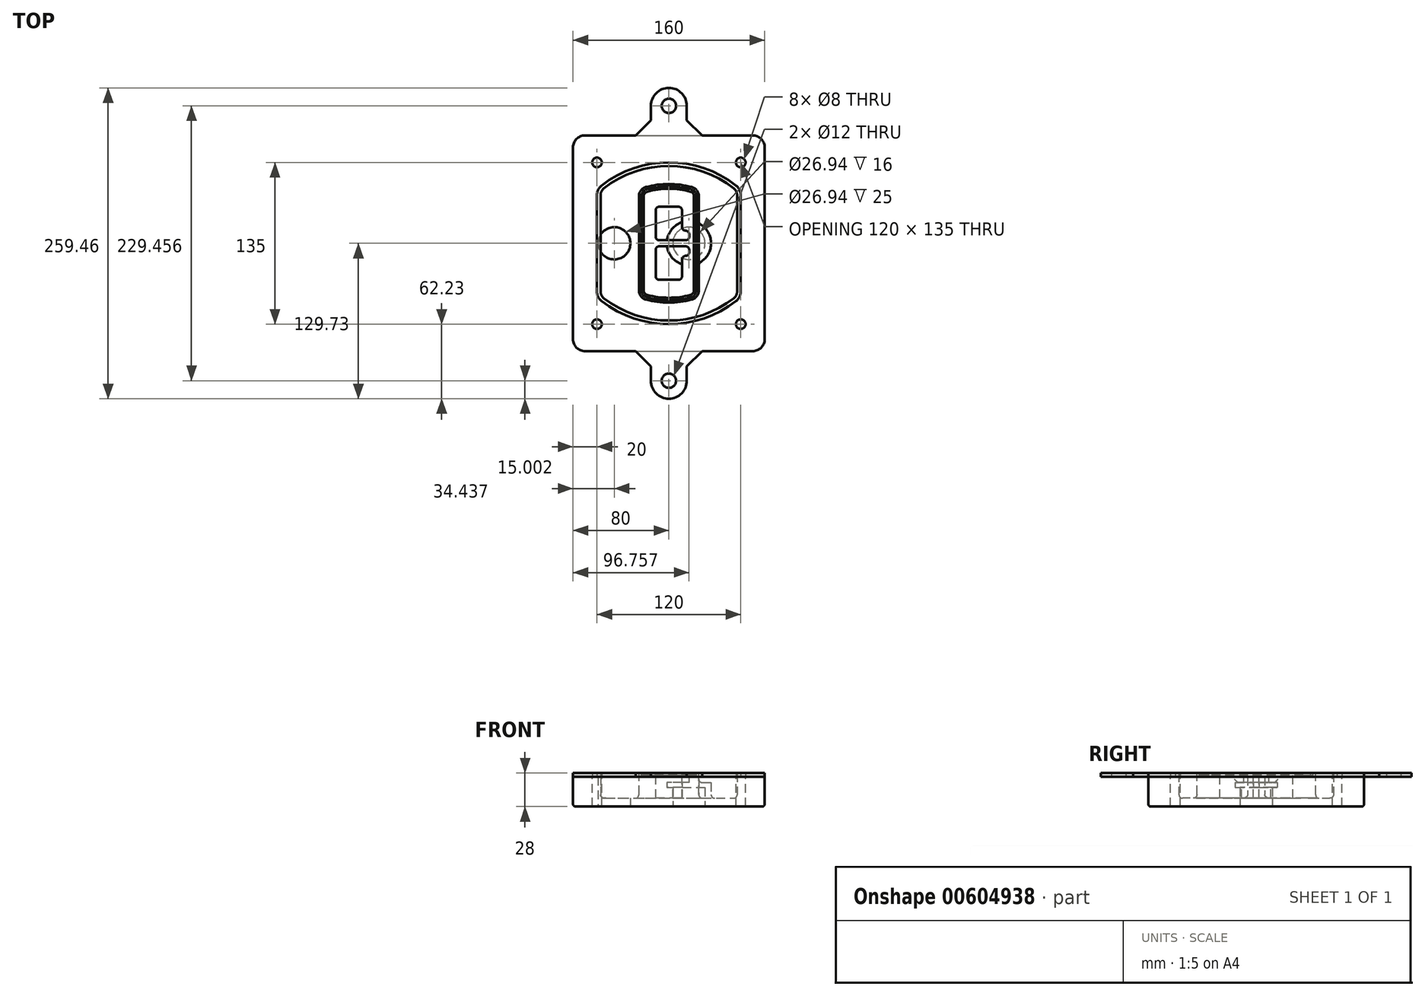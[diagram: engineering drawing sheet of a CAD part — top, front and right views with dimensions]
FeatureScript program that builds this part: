
annotation { "Feature Type Name" : "Feature", "Feature Type Description" : "" }
export const myFeature = defineFeature(function(context is Context, id is Id, definition is map)
    precondition{}
    {
        {
            var Q0;
            Q0=qCreatedBy(makeId("Top.planeOp"),FACE);
            var sketch = newSketch(context, id + "F0", { "sketchPlane" : qUnion([Q0])});
            skPoint(sketch, "E0.rect.middle", {"position": v(0, 0) * mm});
            skLineSegment(sketch, "E1.bottom", {"start": v(-70, -90) * mm, "end": v(70, -90) * mm});
            skLineSegment(sketch, "E1.top", {"start": v(-70, 90) * mm, "end": v(70, 90) * mm});
            skLineSegment(sketch, "E1.left", {"start": v(-80, -80) * mm, "end": v(-80, 80) * mm});
            skLineSegment(sketch, "E1.right", {"start": v(80, -80) * mm, "end": v(80, 80) * mm});
            skLineSegment(sketch, "E2", {"start": v(-80, 90) * mm, "end": v(80, -90) * mm, "construction": true});
            skLineSegment(sketch, "E3", {"start": v(80, 90) * mm, "end": v(-80, -90) * mm, "construction": true});
            skCircle(sketch, "E4", {"center": v(-60, 67.5) * mm, "radius": 4 * mm});
            skCircle(sketch, "E5", {"center": v(60, 67.5) * mm, "radius": 4 * mm});
            skCircle(sketch, "E6", {"center": v(60, -67.5) * mm, "radius": 4 * mm});
            skCircle(sketch, "E7", {"center": v(-60, -67.5) * mm, "radius": 4 * mm});
            skLineSegment(sketch, "E8", {"start": v(-60, 67.5) * mm, "end": v(60, 67.5) * mm, "construction": true});
            skLineSegment(sketch, "E9", {"start": v(60, 67.5) * mm, "end": v(60, -67.5) * mm, "construction": true});
            skLineSegment(sketch, "E10", {"start": v(60, -67.5) * mm, "end": v(-60, -67.5) * mm, "construction": true});
            skLineSegment(sketch, "E11", {"start": v(-60, -67.5) * mm, "end": v(-60, 67.5) * mm, "construction": true});
            skLineSegment(sketch, "E12", {"start": v(-60, 40.3) * mm, "end": v(-60, -40.3) * mm});
            skLineSegment(sketch, "E13", {"start": v(60, 40.3) * mm, "end": v(60, -40.3) * mm});
            skArc(sketch, "E14", {"start": v(56.15, 48.18) * mm, "mid": v(0, 67.5) * mm, "end": v(-56.15, 48.18) * mm});
            skArc(sketch, "E15", {"start": v(-56.15, -48.18) * mm, "mid": v(0, -67.5) * mm, "end": v(56.15, -48.18) * mm});
            skLineSegment(sketch, "E16", {"start": v(-60, 0) * mm, "end": v(60, 0) * mm, "construction": true});
            skPoint(sketch, "E17.visualSharp", {"position": v(-60, -45) * mm});
            skArc(sketch, "E17.filletArc", {"start": v(-60, -40.3) * mm, "mid": v(-58.99, -44.68) * mm, "end": v(-56.15, -48.18) * mm});
            skPoint(sketch, "E18.visualSharp", {"position": v(-60, 45) * mm});
            skArc(sketch, "E18.filletArc", {"start": v(-56.15, 48.18) * mm, "mid": v(-58.99, 44.68) * mm, "end": v(-60, 40.3) * mm});
            skPoint(sketch, "E19.visualSharp", {"position": v(60, 45) * mm});
            skArc(sketch, "E19.filletArc", {"start": v(60, 40.3) * mm, "mid": v(58.99, 44.68) * mm, "end": v(56.15, 48.18) * mm});
            skPoint(sketch, "E20.visualSharp", {"position": v(60, -45) * mm});
            skArc(sketch, "E20.filletArc", {"start": v(56.15, -48.18) * mm, "mid": v(58.99, -44.68) * mm, "end": v(60, -40.3) * mm});
            skPoint(sketch, "E21.visualSharp", {"position": v(-80, 90) * mm});
            skArc(sketch, "E21.filletArc", {"start": v(-70, 90) * mm, "mid": v(-77.07, 87.07) * mm, "end": v(-80, 80) * mm});
            skPoint(sketch, "E22.visualSharp", {"position": v(80, 90) * mm});
            skArc(sketch, "E22.filletArc", {"start": v(80, 80) * mm, "mid": v(77.07, 87.07) * mm, "end": v(70, 90) * mm});
            skPoint(sketch, "E23.visualSharp", {"position": v(80, -90) * mm});
            skArc(sketch, "E23.filletArc", {"start": v(70, -90) * mm, "mid": v(77.07, -87.07) * mm, "end": v(80, -80) * mm});
            skPoint(sketch, "E24.visualSharp", {"position": v(-80, -90) * mm});
            skArc(sketch, "E24.filletArc", {"start": v(-80, -80) * mm, "mid": v(-77.07, -87.07) * mm, "end": v(-70, -90) * mm});
            skArc(sketch, "E25.0", {"start": v(57, 40.3) * mm, "mid": v(56.3, 43.36) * mm, "end": v(54.3, 45.81) * mm});
            skLineSegment(sketch, "E25.1", {"start": v(57, 40.3) * mm, "end": v(57, -40.3) * mm});
            skArc(sketch, "E25.2", {"start": v(54.3, -45.81) * mm, "mid": v(56.3, -43.36) * mm, "end": v(57, -40.3) * mm});
            skArc(sketch, "E25.3", {"start": v(-54.3, -45.81) * mm, "mid": v(0, -64.5) * mm, "end": v(54.3, -45.81) * mm});
            skArc(sketch, "E25.4", {"start": v(-57, -40.3) * mm, "mid": v(-56.3, -43.36) * mm, "end": v(-54.3, -45.81) * mm});
            skArc(sketch, "E25.5", {"start": v(54.3, 45.81) * mm, "mid": v(0, 64.5) * mm, "end": v(-54.3, 45.81) * mm});
            skLineSegment(sketch, "E25.6", {"start": v(-57, 40.3) * mm, "end": v(-57, -40.3) * mm});
            skArc(sketch, "E25.7", {"start": v(-54.3, 45.81) * mm, "mid": v(-56.3, 43.36) * mm, "end": v(-57, 40.3) * mm});
            skArc(sketch, "E26.0", {"start": v(-58.62, 51.33) * mm, "mid": v(-62.58, 46.43) * mm, "end": v(-64, 40.3) * mm});
            skArc(sketch, "E26.1", {"start": v(58.62, 51.33) * mm, "mid": v(0, 71.5) * mm, "end": v(-58.62, 51.33) * mm});
            skArc(sketch, "E26.2", {"start": v(64, 40.3) * mm, "mid": v(62.58, 46.43) * mm, "end": v(58.62, 51.33) * mm});
            skLineSegment(sketch, "E26.3", {"start": v(64, 40.3) * mm, "end": v(64, -40.3) * mm});
            skArc(sketch, "E26.4", {"start": v(58.62, -51.33) * mm, "mid": v(62.58, -46.43) * mm, "end": v(64, -40.3) * mm});
            skLineSegment(sketch, "E26.5", {"start": v(-64, 40.3) * mm, "end": v(-64, -40.3) * mm});
            skArc(sketch, "E26.6", {"start": v(-58.62, -51.33) * mm, "mid": v(0, -71.5) * mm, "end": v(58.62, -51.33) * mm});
            skArc(sketch, "E26.7", {"start": v(-64, -40.3) * mm, "mid": v(-62.58, -46.43) * mm, "end": v(-58.62, -51.33) * mm});
            skSolve(sketch);
        }
        {
            var Q0;
            Q0=makeQuery(id+"F0.imprint","IMPRINT",FACE,{"disambiguationData":[TD([[makeQuery(id+"F0.imprint","IMPRINT",EDGE,{"derivedFrom":sQuery(id+"F0.wireOp",EDGE,"E1.bottom")}),1.0]])]});
            var Q1;
            Q1=makeQuery(id+"F0.imprint","IMPRINT",FACE,{"disambiguationData":[TD([[makeQuery(id+"F0.imprint","IMPRINT",EDGE,{"derivedFrom":sQuery(id+"F0.wireOp",EDGE,"E12")}),1.0]])]});
            var Q2;
            Q2=makeQuery(id+"F0.imprint","IMPRINT",FACE,{"disambiguationData":[TD([[makeQuery(id+"F0.imprint","IMPRINT",EDGE,{"derivedFrom":sQuery(id+"F0.wireOp",EDGE,"E25.0")}),1.0]])]});
            var Q3;
            Q3=makeQuery(id+"F0.imprint","IMPRINT",FACE,{"disambiguationData":[TD([[makeQuery(id+"F0.imprint","IMPRINT",EDGE,{"derivedFrom":sQuery(id+"F0.wireOp",EDGE,"E12")}),-1.0]])]});
            extrude(context, id + "F1", {"entities" : qUnion([Q0, Q1, Q2, Q3]), "oppositeDirection" : true, "depth" : 25 * mm});
        }
        {
            var Q0;
            Q0=makeQuery(id+"F0.imprint","IMPRINT",FACE,{"disambiguationData":[TD([[makeQuery(id+"F0.imprint","IMPRINT",EDGE,{"derivedFrom":sQuery(id+"F0.wireOp",EDGE,"E12")}),1.0]])]});
            extrude(context, id + "F2", {"entities" : qUnion([Q0]), "operationType" : NewBodyOperationType.ADD, "depth" : 3 * mm});
        }
        {
            var Q0;
            Q0=makeQuery(id+"F0.imprint","IMPRINT",FACE,{"disambiguationData":[TD([[makeQuery(id+"F0.imprint","IMPRINT",EDGE,{"derivedFrom":sQuery(id+"F0.wireOp",EDGE,"E25.0")}),1.0]])]});
            extrude(context, id + "F3", {"entities" : qUnion([Q0]), "operationType" : NewBodyOperationType.REMOVE, "oppositeDirection" : true, "depth" : 18 * mm});
        }
        {
            var Q0;
            Q0=makeQuery(id+"F2.opExtrude","CAP_FACE",FACE,{"disambiguationData":[OSD([sQuery(id+"F0.wireOp",EDGE,"E12"),sQuery(id+"F0.wireOp",EDGE,"E13"),sQuery(id+"F0.wireOp",EDGE,"E14"),sQuery(id+"F0.wireOp",EDGE,"E15"),sQuery(id+"F0.wireOp",EDGE,"E17.filletArc"),sQuery(id+"F0.wireOp",EDGE,"E18.filletArc"),sQuery(id+"F0.wireOp",EDGE,"E19.filletArc"),sQuery(id+"F0.wireOp",EDGE,"E20.filletArc"),sQuery(id+"F0.wireOp",EDGE,"E25.0"),sQuery(id+"F0.wireOp",EDGE,"E25.1"),sQuery(id+"F0.wireOp",EDGE,"E25.2"),sQuery(id+"F0.wireOp",EDGE,"E25.3"),sQuery(id+"F0.wireOp",EDGE,"E25.4"),sQuery(id+"F0.wireOp",EDGE,"E25.5"),sQuery(id+"F0.wireOp",EDGE,"E25.6"),sQuery(id+"F0.wireOp",EDGE,"E25.7")])],"isStart":false});
            var sketch = newSketch(context, id + "F4", { "sketchPlane" : qUnion([Q0])});
            skArc(sketch, "E27.0", {"start": v(-19.08, -46.97) * mm, "mid": v(0, -49.5) * mm, "end": v(19.08, -46.97) * mm});
            skArc(sketch, "E28.0", {"start": v(19.08, 46.97) * mm, "mid": v(0, 49.5) * mm, "end": v(-19.08, 46.97) * mm});
            skLineSegment(sketch, "E29", {"start": v(-25, 39.25) * mm, "end": v(-25, -39.25) * mm});
            skLineSegment(sketch, "E30", {"start": v(25, 39.25) * mm, "end": v(25, -39.25) * mm});
            skLineSegment(sketch, "E31", {"start": v(-25, 45.1) * mm, "end": v(25, 45.1) * mm, "construction": true});
            skLineSegment(sketch, "E32", {"start": v(-25, -45.1) * mm, "end": v(25, -45.1) * mm, "construction": true});
            skPoint(sketch, "E33.visualSharp", {"position": v(-25, 45.1) * mm});
            skArc(sketch, "E33.filletArc", {"start": v(-19.08, 46.97) * mm, "mid": v(-23.35, 44.11) * mm, "end": v(-25, 39.25) * mm});
            skPoint(sketch, "E34.visualSharp", {"position": v(25, 45.1) * mm});
            skArc(sketch, "E34.filletArc", {"start": v(25, 39.25) * mm, "mid": v(23.35, 44.11) * mm, "end": v(19.08, 46.97) * mm});
            skPoint(sketch, "E35.visualSharp", {"position": v(25, -45.1) * mm});
            skArc(sketch, "E35.filletArc", {"start": v(19.08, -46.97) * mm, "mid": v(23.35, -44.11) * mm, "end": v(25, -39.25) * mm});
            skPoint(sketch, "E36.visualSharp", {"position": v(-25, -45.1) * mm});
            skArc(sketch, "E36.filletArc", {"start": v(-25, -39.25) * mm, "mid": v(-23.35, -44.11) * mm, "end": v(-19.08, -46.97) * mm});
            skArc(sketch, "E37.0", {"start": v(54.3, 45.81) * mm, "mid": v(0, 64.5) * mm, "end": v(-54.3, 45.81) * mm});
            skArc(sketch, "E37.1", {"start": v(-54.3, 45.81) * mm, "mid": v(-56.3, 43.36) * mm, "end": v(-57, 40.3) * mm});
            skLineSegment(sketch, "E37.2", {"start": v(-57, 40.3) * mm, "end": v(-57, -40.3) * mm});
            skArc(sketch, "E37.3", {"start": v(-57, -40.3) * mm, "mid": v(-56.3, -43.36) * mm, "end": v(-54.3, -45.81) * mm});
            skArc(sketch, "E37.4", {"start": v(-54.3, -45.81) * mm, "mid": v(0, -64.5) * mm, "end": v(54.3, -45.81) * mm});
            skArc(sketch, "E37.5", {"start": v(54.3, -45.81) * mm, "mid": v(56.3, -43.36) * mm, "end": v(57, -40.3) * mm});
            skLineSegment(sketch, "E37.6", {"start": v(57, 40.3) * mm, "end": v(57, -40.3) * mm});
            skArc(sketch, "E37.7", {"start": v(57, 40.3) * mm, "mid": v(56.3, 43.36) * mm, "end": v(54.3, 45.81) * mm});
            skLineSegment(sketch, "E38.0", {"start": v(23, 39.25) * mm, "end": v(23, -39.25) * mm});
            skArc(sketch, "E38.1", {"start": v(18.56, -45.04) * mm, "mid": v(21.76, -42.9) * mm, "end": v(23, -39.25) * mm});
            skArc(sketch, "E38.2", {"start": v(-18.56, -45.04) * mm, "mid": v(0, -47.5) * mm, "end": v(18.56, -45.04) * mm});
            skArc(sketch, "E38.3", {"start": v(-23, -39.25) * mm, "mid": v(-21.76, -42.9) * mm, "end": v(-18.56, -45.04) * mm});
            skLineSegment(sketch, "E38.4", {"start": v(-23, 39.25) * mm, "end": v(-23, -39.25) * mm});
            skArc(sketch, "E38.5", {"start": v(23, 39.25) * mm, "mid": v(21.76, 42.9) * mm, "end": v(18.56, 45.04) * mm});
            skArc(sketch, "E38.6", {"start": v(-18.56, 45.04) * mm, "mid": v(-21.76, 42.9) * mm, "end": v(-23, 39.25) * mm});
            skArc(sketch, "E38.7", {"start": v(18.56, 45.04) * mm, "mid": v(0, 47.5) * mm, "end": v(-18.56, 45.04) * mm});
            skArc(sketch, "E39.0", {"start": v(21, 39.25) * mm, "mid": v(20.18, 41.68) * mm, "end": v(18.04, 43.1) * mm});
            skLineSegment(sketch, "E39.1", {"start": v(21, 39.25) * mm, "end": v(21, -39.25) * mm});
            skArc(sketch, "E39.2", {"start": v(18.04, -43.1) * mm, "mid": v(20.18, -41.68) * mm, "end": v(21, -39.25) * mm});
            skArc(sketch, "E39.3", {"start": v(-18.04, -43.1) * mm, "mid": v(0, -45.5) * mm, "end": v(18.04, -43.1) * mm});
            skArc(sketch, "E39.4", {"start": v(-21, -39.25) * mm, "mid": v(-20.18, -41.68) * mm, "end": v(-18.04, -43.1) * mm});
            skArc(sketch, "E39.5", {"start": v(18.04, 43.1) * mm, "mid": v(0, 45.5) * mm, "end": v(-18.04, 43.1) * mm});
            skLineSegment(sketch, "E39.6", {"start": v(-21, 39.25) * mm, "end": v(-21, -39.25) * mm});
            skArc(sketch, "E39.7", {"start": v(-18.04, 43.1) * mm, "mid": v(-20.18, 41.68) * mm, "end": v(-21, 39.25) * mm});
            skLineSegment(sketch, "E40", {"start": v(-25, 0) * mm, "end": v(25, 0) * mm, "construction": true});
            skLineSegment(sketch, "E41", {"start": v(-11, 5.5) * mm, "end": v(-11, 27.5) * mm});
            skLineSegment(sketch, "E42", {"start": v(-8, 30.5) * mm, "end": v(8, 30.5) * mm});
            skLineSegment(sketch, "E43", {"start": v(11, 27.5) * mm, "end": v(11, 13.5) * mm});
            skLineSegment(sketch, "E44", {"start": v(14, 10.5) * mm, "end": v(14, 10.5) * mm});
            skLineSegment(sketch, "E45", {"start": v(17, 7.5) * mm, "end": v(17, 5.5) * mm});
            skLineSegment(sketch, "E46", {"start": v(14, 2.5) * mm, "end": v(-8, 2.5) * mm});
            skPoint(sketch, "E47.visualSharp", {"position": v(-11, 30.5) * mm});
            skArc(sketch, "E47.filletArc", {"start": v(-8, 30.5) * mm, "mid": v(-10.12, 29.62) * mm, "end": v(-11, 27.5) * mm});
            skPoint(sketch, "E48.visualSharp", {"position": v(11, 30.5) * mm});
            skArc(sketch, "E48.filletArc", {"start": v(11, 27.5) * mm, "mid": v(10.12, 29.62) * mm, "end": v(8, 30.5) * mm});
            skPoint(sketch, "E49.visualSharp", {"position": v(11, 10.5) * mm});
            skArc(sketch, "E49.filletArc", {"start": v(11, 13.5) * mm, "mid": v(11.88, 11.38) * mm, "end": v(14, 10.5) * mm});
            skPoint(sketch, "E50.visualSharp", {"position": v(17, 10.5) * mm});
            skArc(sketch, "E50.filletArc", {"start": v(17, 7.5) * mm, "mid": v(16.12, 9.62) * mm, "end": v(14, 10.5) * mm});
            skPoint(sketch, "E51.visualSharp", {"position": v(17, 2.5) * mm});
            skArc(sketch, "E51.filletArc", {"start": v(14, 2.5) * mm, "mid": v(16.12, 3.38) * mm, "end": v(17, 5.5) * mm});
            skPoint(sketch, "E52.visualSharp", {"position": v(-11, 2.5) * mm});
            skArc(sketch, "E52.filletArc", {"start": v(-11, 5.5) * mm, "mid": v(-10.12, 3.38) * mm, "end": v(-8, 2.5) * mm});
            skLineSegment(sketch, "E53.0.MirrorCS", {"start": v(14, -2.5) * mm, "end": v(-8, -2.5) * mm});
            skArc(sketch, "E54.0.MirrorCS", {"start": v(-11, -5.5) * mm, "mid": v(-10.12, -3.38) * mm, "end": v(-8, -2.5) * mm});
            skLineSegment(sketch, "E55.0.MirrorCS", {"start": v(-11, -5.5) * mm, "end": v(-11, -27.5) * mm});
            skArc(sketch, "E56.0.MirrorCS", {"start": v(-8, -30.5) * mm, "mid": v(-10.12, -29.62) * mm, "end": v(-11, -27.5) * mm});
            skLineSegment(sketch, "E57.0.MirrorCS", {"start": v(-8, -30.5) * mm, "end": v(8, -30.5) * mm});
            skArc(sketch, "E58.0.MirrorCS", {"start": v(11, -27.5) * mm, "mid": v(10.12, -29.62) * mm, "end": v(8, -30.5) * mm});
            skLineSegment(sketch, "E59.0.MirrorCS", {"start": v(11, -27.5) * mm, "end": v(11, -13.5) * mm});
            skArc(sketch, "E60.0.MirrorCS", {"start": v(11, -13.5) * mm, "mid": v(11.88, -11.38) * mm, "end": v(14, -10.5) * mm});
            skArc(sketch, "E61.0.MirrorCS", {"start": v(17, -7.5) * mm, "mid": v(16.12, -9.62) * mm, "end": v(14, -10.5) * mm});
            skLineSegment(sketch, "E62.0.MirrorCS", {"start": v(17, -7.5) * mm, "end": v(17, -5.5) * mm});
            skArc(sketch, "E63.0.MirrorCS", {"start": v(14, -2.5) * mm, "mid": v(16.12, -3.38) * mm, "end": v(17, -5.5) * mm});
            skSolve(sketch);
        }
        {
            var Q0;
            Q0=makeQuery(id+"F4.imprint","IMPRINT",FACE,{"disambiguationData":[TD([[makeQuery(id+"F4.imprint","IMPRINT",EDGE,{"derivedFrom":sQuery(id+"F4.wireOp",EDGE,"E27.0")}),1.0]])]});
            var Q1;
            Q1=makeQuery(id+"F4.imprint","IMPRINT",FACE,{"disambiguationData":[TD([[makeQuery(id+"F4.imprint","IMPRINT",EDGE,{"derivedFrom":sQuery(id+"F4.wireOp",EDGE,"E38.0")}),-1.0]])]});
            var Q2;
            Q2=makeQuery(id+"F4.imprint","IMPRINT",FACE,{"disambiguationData":[TD([[makeQuery(id+"F4.imprint","IMPRINT",EDGE,{"derivedFrom":sQuery(id+"F4.wireOp",EDGE,"E39.0")}),1.0]])]});
            extrude(context, id + "F5", {"entities" : qUnion([Q0, Q1, Q2]), "operationType" : NewBodyOperationType.ADD, "endBound" : BoundingType.UP_TO_NEXT, "oppositeDirection" : true, "depth" : 25 * mm});
        }
        {
            var Q0;
            Q0=makeQuery(id+"F4.imprint","IMPRINT",FACE,{"disambiguationData":[TD([[makeQuery(id+"F4.imprint","IMPRINT",EDGE,{"derivedFrom":sQuery(id+"F4.wireOp",EDGE,"E38.0")}),-1.0]])]});
            extrude(context, id + "F6", {"entities" : qUnion([Q0]), "operationType" : NewBodyOperationType.REMOVE, "oppositeDirection" : true, "depth" : 2 * mm});
        }
        {
            var Q0;
            Q0=makeQuery(id+"F1.opExtrude","CAP_FACE",FACE,{"disambiguationData":[OSD([sQuery(id+"F0.wireOp",EDGE,"E1.bottom"),sQuery(id+"F0.wireOp",EDGE,"E1.top"),sQuery(id+"F0.wireOp",EDGE,"E1.left"),sQuery(id+"F0.wireOp",EDGE,"E1.right"),sQuery(id+"F0.wireOp",EDGE,"E4"),sQuery(id+"F0.wireOp",EDGE,"E5"),sQuery(id+"F0.wireOp",EDGE,"E6"),sQuery(id+"F0.wireOp",EDGE,"E7"),sQuery(id+"F0.wireOp",EDGE,"E21.filletArc"),sQuery(id+"F0.wireOp",EDGE,"E22.filletArc"),sQuery(id+"F0.wireOp",EDGE,"E23.filletArc"),sQuery(id+"F0.wireOp",EDGE,"E24.filletArc")])],"isStart":false});
            var sketch = newSketch(context, id + "F7", { "sketchPlane" : qUnion([Q0])});
            skCircle(sketch, "E64", {"center": v(16.76, 0) * mm, "radius": 13.47 * mm});
            skCircle(sketch, "E65", {"center": v(-45.56, 0) * mm, "radius": 13.47 * mm});
            skLineSegment(sketch, "E66", {"start": v(80, 0) * mm, "end": v(-80, 0) * mm});
            skCircle(sketch, "E67", {"center": v(16.76, 0) * mm, "radius": 18.47 * mm});
            skCircle(sketch, "E68", {"center": v(60, -67.5) * mm, "radius": 6 * mm});
            skCircle(sketch, "E69", {"center": v(-60, -67.5) * mm, "radius": 6 * mm});
            skCircle(sketch, "E70", {"center": v(-60, 67.5) * mm, "radius": 6 * mm});
            skCircle(sketch, "E71", {"center": v(60, 67.5) * mm, "radius": 6 * mm});
            skSolve(sketch);
        }
        {
            var Q0;
            {var subQ1=sQuery(id+"F7.wireOp",EDGE,"E66");var subQ4=sQuery(id+"F7.wireOp",EDGE,"E64");var subQ6=makeQuery(id+"F7.imprint","INTERSECT",VERTEX,{"disambiguationData":[OD(0.0)],"derivedFrom":[subQ4,subQ1]});Q0=makeQuery(id+"F7.imprint","IMPRINT",FACE,{"disambiguationData":[TD([[makeQuery(id+"F7.imprint","IMPRINT",EDGE,{"disambiguationData":[TD([[subQ6,-1.0]])],"derivedFrom":subQ4}),-1.0]])]});}
            var Q1;
            {var subQ0=sQuery(id+"F7.wireOp",EDGE,"E66");var subQ1=sQuery(id+"F7.wireOp",EDGE,"E64");var subQ3=makeQuery(id+"F7.imprint","INTERSECT",VERTEX,{"disambiguationData":[OD(0.0)],"derivedFrom":[subQ1,subQ0]});Q1=makeQuery(id+"F7.imprint","IMPRINT",FACE,{"disambiguationData":[TD([[makeQuery(id+"F7.imprint","IMPRINT",EDGE,{"disambiguationData":[TD([[subQ3,-1.0]])],"derivedFrom":subQ1}),1.0]])]});}
            var Q2;
            {var subQ0=sQuery(id+"F7.wireOp",EDGE,"E66");var subQ1=sQuery(id+"F7.wireOp",EDGE,"E64");var subQ3=makeQuery(id+"F7.imprint","INTERSECT",VERTEX,{"disambiguationData":[OD(0.0)],"derivedFrom":[subQ1,subQ0]});Q2=makeQuery(id+"F7.imprint","IMPRINT",FACE,{"disambiguationData":[TD([[makeQuery(id+"F7.imprint","IMPRINT",EDGE,{"disambiguationData":[TD([[subQ3,1.0]])],"derivedFrom":subQ1}),1.0]])]});}
            var Q3;
            {var subQ1=sQuery(id+"F7.wireOp",EDGE,"E66");var subQ4=sQuery(id+"F7.wireOp",EDGE,"E64");var subQ6=makeQuery(id+"F7.imprint","INTERSECT",VERTEX,{"disambiguationData":[OD(0.0)],"derivedFrom":[subQ4,subQ1]});Q3=makeQuery(id+"F7.imprint","IMPRINT",FACE,{"disambiguationData":[TD([[makeQuery(id+"F7.imprint","IMPRINT",EDGE,{"disambiguationData":[TD([[subQ6,1.0]])],"derivedFrom":subQ4}),-1.0]])]});}
            extrude(context, id + "F8", {"entities" : qUnion([Q0, Q1, Q2, Q3]), "operationType" : NewBodyOperationType.ADD, "oppositeDirection" : true, "depth" : 20 * mm});
        }
        {
            var Q0;
            {var subQ0=sQuery(id+"F7.wireOp",EDGE,"E66");var subQ1=sQuery(id+"F7.wireOp",EDGE,"E64");var subQ3=makeQuery(id+"F7.imprint","INTERSECT",VERTEX,{"disambiguationData":[OD(0.0)],"derivedFrom":[subQ1,subQ0]});Q0=makeQuery(id+"F7.imprint","IMPRINT",FACE,{"disambiguationData":[TD([[makeQuery(id+"F7.imprint","IMPRINT",EDGE,{"disambiguationData":[TD([[subQ3,-1.0]])],"derivedFrom":subQ1}),1.0]])]});}
            var Q1;
            {var subQ0=sQuery(id+"F7.wireOp",EDGE,"E66");var subQ1=sQuery(id+"F7.wireOp",EDGE,"E64");var subQ3=makeQuery(id+"F7.imprint","INTERSECT",VERTEX,{"disambiguationData":[OD(0.0)],"derivedFrom":[subQ1,subQ0]});Q1=makeQuery(id+"F7.imprint","IMPRINT",FACE,{"disambiguationData":[TD([[makeQuery(id+"F7.imprint","IMPRINT",EDGE,{"disambiguationData":[TD([[subQ3,1.0]])],"derivedFrom":subQ1}),1.0]])]});}
            extrude(context, id + "F9", {"entities" : qUnion([Q0, Q1]), "operationType" : NewBodyOperationType.REMOVE, "oppositeDirection" : true, "depth" : 16 * mm});
        }
        {
            var Q0;
            {var subQ0=sQuery(id+"F7.wireOp",EDGE,"E66");var subQ1=sQuery(id+"F7.wireOp",EDGE,"E65");var subQ3=makeQuery(id+"F7.imprint","INTERSECT",VERTEX,{"disambiguationData":[OD(0.0)],"derivedFrom":[subQ1,subQ0]});Q0=makeQuery(id+"F7.imprint","IMPRINT",FACE,{"disambiguationData":[TD([[makeQuery(id+"F7.imprint","IMPRINT",EDGE,{"disambiguationData":[TD([[subQ3,-1.0]])],"derivedFrom":subQ1}),1.0]])]});}
            var Q1;
            {var subQ0=sQuery(id+"F7.wireOp",EDGE,"E66");var subQ1=sQuery(id+"F7.wireOp",EDGE,"E65");var subQ3=makeQuery(id+"F7.imprint","INTERSECT",VERTEX,{"disambiguationData":[OD(0.0)],"derivedFrom":[subQ1,subQ0]});Q1=makeQuery(id+"F7.imprint","IMPRINT",FACE,{"disambiguationData":[TD([[makeQuery(id+"F7.imprint","IMPRINT",EDGE,{"disambiguationData":[TD([[subQ3,1.0]])],"derivedFrom":subQ1}),1.0]])]});}
            extrude(context, id + "F10", {"entities" : qUnion([Q0, Q1]), "operationType" : NewBodyOperationType.REMOVE, "oppositeDirection" : true, "depth" : 25 * mm});
        }
        {
            var Q0;
            Q0=makeQuery(id+"F9.boolean.opBoolean","COPY",FACE,{"derivedFrom":makeQuery(id+"F9.opExtrude","CAP_FACE",FACE,{"disambiguationData":[OSD([sQuery(id+"F7.wireOp",EDGE,"E64")])],"isStart":false})});
            var sketch = newSketch(context, id + "F11", { "sketchPlane" : qUnion([Q0])});
            skArc(sketch, "E72.0", {"start": v(11, 17.55) * mm, "mid": v(2.57, 11.82) * mm, "end": v(-1.54, 2.5) * mm});
            skArc(sketch, "E72.1", {"start": v(-1.54, -2.5) * mm, "mid": v(2.57, -11.82) * mm, "end": v(11, -17.55) * mm});
            skLineSegment(sketch, "E73", {"start": v(-1.54, -2.5) * mm, "end": v(14, -2.5) * mm});
            skLineSegment(sketch, "E74.0", {"start": v(14, 2.5) * mm, "end": v(-1.54, 2.5) * mm});
            skArc(sketch, "E74.1", {"start": v(14, 2.5) * mm, "mid": v(16.12, 3.38) * mm, "end": v(17, 5.5) * mm});
            skLineSegment(sketch, "E74.2", {"start": v(17, 7.5) * mm, "end": v(17, 5.5) * mm});
            skArc(sketch, "E74.3", {"start": v(17, 7.5) * mm, "mid": v(16.12, 9.62) * mm, "end": v(14, 10.5) * mm});
            skArc(sketch, "E74.4", {"start": v(11, 13.5) * mm, "mid": v(11.88, 11.38) * mm, "end": v(14, 10.5) * mm});
            skLineSegment(sketch, "E74.5", {"start": v(11, 17.55) * mm, "end": v(11, 13.5) * mm});
            skLineSegment(sketch, "E74.7", {"start": v(14, -2.5) * mm, "end": v(-1.54, -2.5) * mm});
            skArc(sketch, "E74.8", {"start": v(14, -2.5) * mm, "mid": v(16.12, -3.38) * mm, "end": v(17, -5.5) * mm});
            skLineSegment(sketch, "E74.9", {"start": v(17, -7.5) * mm, "end": v(17, -5.5) * mm});
            skArc(sketch, "E74.10", {"start": v(17, -7.5) * mm, "mid": v(16.12, -9.62) * mm, "end": v(14, -10.5) * mm});
            skArc(sketch, "E74.11", {"start": v(11, -13.5) * mm, "mid": v(11.88, -11.38) * mm, "end": v(14, -10.5) * mm});
            skLineSegment(sketch, "E74.12", {"start": v(11, -17.55) * mm, "end": v(11, -13.5) * mm});
            skPoint(sketch, "E75.orphan", {"position": v(11, -27.5) * mm});
            skPoint(sketch, "E76.orphan", {"position": v(-8, -2.5) * mm});
            skPoint(sketch, "E77.orphan", {"position": v(-8, 2.5) * mm});
            skPoint(sketch, "E78.orphan", {"position": v(11, 27.5) * mm});
            skSolve(sketch);
        }
        {
            var Q0;
            {var subQ7=sQuery(id+"F11.wireOp",EDGE,"E72.0");var subQ14=sQuery(id+"F11.wireOp",EDGE,"E72.1");var subQ16=sQuery(id+"F11.wireOp",EDGE,"E74.1");var subQ18=sQuery(id+"F11.wireOp",EDGE,"E74.8");Q0=qUnion([makeQuery(id+"F11.imprint","IMPRINT",FACE,{"disambiguationData":[TD([[makeQuery(id+"F11.imprint","IMPRINT",EDGE,{"derivedFrom":subQ7}),1.0]])]}),makeQuery(id+"F11.imprint","IMPRINT",FACE,{"disambiguationData":[TD([[makeQuery(id+"F11.imprint","IMPRINT",EDGE,{"derivedFrom":subQ14}),1.0]])]}),makeQuery(id+"F11.imprint","IMPRINT",FACE,{"disambiguationData":[TD([[makeQuery(id+"F11.imprint","IMPRINT",EDGE,{"derivedFrom":subQ16}),1.0]])]}),makeQuery(id+"F11.imprint","IMPRINT",FACE,{"disambiguationData":[TD([[makeQuery(id+"F11.imprint","IMPRINT",EDGE,{"derivedFrom":subQ18}),-1.0]])]})]);}
            var Q1;
            Q1=makeQuery(id+"F5.boolean.opBoolean","SPLIT",FACE,{"disambiguationData":[TD([makeQuery(id+"F5.opExtrude","SWEPT_FACE",FACE,{"disambiguationData":[OSD([sQuery(id+"F4.wireOp",EDGE,"E41")])]})])],"derivedFrom":makeQuery(id+"F3.boolean.opBoolean","COPY",FACE,{"derivedFrom":makeQuery(id+"F3.opExtrude","CAP_FACE",FACE,{"disambiguationData":[OSD([sQuery(id+"F0.wireOp",EDGE,"E25.0"),sQuery(id+"F0.wireOp",EDGE,"E25.1"),sQuery(id+"F0.wireOp",EDGE,"E25.2"),sQuery(id+"F0.wireOp",EDGE,"E25.3"),sQuery(id+"F0.wireOp",EDGE,"E25.4"),sQuery(id+"F0.wireOp",EDGE,"E25.5"),sQuery(id+"F0.wireOp",EDGE,"E25.6"),sQuery(id+"F0.wireOp",EDGE,"E25.7")])],"isStart":false})})});
            extrude(context, id + "F12", {"entities" : qUnion([Q0]), "operationType" : NewBodyOperationType.REMOVE, "endBound" : BoundingType.UP_TO_SURFACE, "endBoundEntityFace" : qUnion([Q1]), "depth" : 25 * mm});
        }
        {
            var Q0;
            Q0=makeQuery(id+"F3.boolean.opBoolean","COPY",EDGE,{"derivedFrom":makeQuery(id+"F3.opExtrude","CAP_EDGE",EDGE,{"disambiguationData":[OSD([sQuery(id+"F0.wireOp",EDGE,"E25.6")])],"isStart":false})});
            var Q1;
            Q1=makeQuery(id+"F8.boolean.opBoolean","INTERSECT",EDGE,{"derivedFrom":[makeQuery(id+"F5.opExtrude","SWEPT_FACE",FACE,{"disambiguationData":[OSD([sQuery(id+"F4.wireOp",EDGE,"E30")])]}),makeQuery(id+"F8.opExtrude","CAP_FACE",FACE,{"disambiguationData":[OSD([sQuery(id+"F7.wireOp",EDGE,"E67")])],"isStart":false})]});
            var Q2;
            Q2=makeQuery(id+"F8.boolean.opBoolean","INTERSECT",EDGE,{"disambiguationData":[OD(1.0)],"derivedFrom":[makeQuery(id+"F5.opExtrude","SWEPT_FACE",FACE,{"disambiguationData":[OSD([sQuery(id+"F4.wireOp",EDGE,"E30")])]}),makeQuery(id+"F8.opExtrude","SWEPT_FACE",FACE,{"disambiguationData":[OSD([sQuery(id+"F7.wireOp",EDGE,"E67")])]})]});
            var Q3;
            {var subQ0=sQuery(id+"F4.wireOp",EDGE,"E30");Q3=makeQuery(id+"F8.boolean.opBoolean","SPLIT",EDGE,{"disambiguationData":[TD([makeQuery(id+"F5.opExtrude","SWEPT_FACE",FACE,{"disambiguationData":[OSD([sQuery(id+"F4.wireOp",EDGE,"E35.filletArc")])]})])],"derivedFrom":makeQuery(id+"F5.opExtrude","CAP_EDGE",EDGE,{"disambiguationData":[OSD([subQ0])],"isStart":false})});}
            var Q4;
            {var subQ0=sQuery(id+"F0.wireOp",EDGE,"E25.7");var subQ1=sQuery(id+"F0.wireOp",EDGE,"E25.1");var subQ2=sQuery(id+"F0.wireOp",EDGE,"E25.6");var subQ3=sQuery(id+"F0.wireOp",EDGE,"E25.5");var subQ4=sQuery(id+"F0.wireOp",EDGE,"E25.4");var subQ5=sQuery(id+"F0.wireOp",EDGE,"E25.0");var subQ6=sQuery(id+"F0.wireOp",EDGE,"E25.2");var subQ7=sQuery(id+"F0.wireOp",EDGE,"E25.3");Q4=makeQuery(id+"F8.boolean.opBoolean","INTERSECT",EDGE,{"derivedFrom":[makeQuery(id+"F5.boolean.opBoolean","SPLIT",FACE,{"disambiguationData":[TD([makeQuery(id+"F2.opExtrude","SWEPT_FACE",FACE,{"disambiguationData":[OSD([subQ5])]})])],"derivedFrom":makeQuery(id+"F3.boolean.opBoolean","COPY",FACE,{"derivedFrom":makeQuery(id+"F3.opExtrude","CAP_FACE",FACE,{"disambiguationData":[OSD([subQ5,subQ1,subQ6,subQ7,subQ4,subQ3,subQ2,subQ0])],"isStart":false})})}),makeQuery(id+"F8.opExtrude","SWEPT_FACE",FACE,{"disambiguationData":[OSD([sQuery(id+"F7.wireOp",EDGE,"E67")])]})]});}
            var Q5;
            Q5=makeQuery(id+"F8.boolean.opBoolean","INTERSECT",EDGE,{"disambiguationData":[OD(0.0)],"derivedFrom":[makeQuery(id+"F5.opExtrude","SWEPT_FACE",FACE,{"disambiguationData":[OSD([sQuery(id+"F4.wireOp",EDGE,"E30")])]}),makeQuery(id+"F8.opExtrude","SWEPT_FACE",FACE,{"disambiguationData":[OSD([sQuery(id+"F7.wireOp",EDGE,"E67")])]})]});
            fillet(context, id + "F13", {"entities" : qUnion([Q0, Q1, Q2, Q3, Q4, Q5]), "radius" : 3 * mm, "tangentPropagation" : true, "allowEdgeOverflow" : false});
        }
        {
            var Q0;
            Q0=makeQuery(id+"F1.opExtrude","CAP_EDGE",EDGE,{"disambiguationData":[OSD([sQuery(id+"F0.wireOp",EDGE,"E1.bottom")])],"isStart":false});
            fillet(context, id + "F14", {"entities" : qUnion([Q0]), "radius" : 2 * mm, "tangentPropagation" : true, "allowEdgeOverflow" : false});
        }
        {
            var Q0;
            {var subQ0=sQuery(id+"F0.wireOp",EDGE,"E21.filletArc");var subQ1=sQuery(id+"F0.wireOp",EDGE,"E7");var subQ2=sQuery(id+"F0.wireOp",EDGE,"E6");var subQ3=sQuery(id+"F0.wireOp",EDGE,"E5");var subQ4=sQuery(id+"F0.wireOp",EDGE,"E4");var subQ5=sQuery(id+"F0.wireOp",EDGE,"E22.filletArc");var subQ6=sQuery(id+"F0.wireOp",EDGE,"E1.bottom");var subQ7=sQuery(id+"F0.wireOp",EDGE,"E1.right");var subQ8=sQuery(id+"F0.wireOp",EDGE,"E1.top");var subQ9=sQuery(id+"F0.wireOp",EDGE,"E1.left");var subQ10=sQuery(id+"F0.wireOp",EDGE,"E23.filletArc");var subQ11=sQuery(id+"F0.wireOp",EDGE,"E24.filletArc");Q0=makeQuery(id+"F2.boolean.opBoolean","SPLIT",FACE,{"disambiguationData":[TD([makeQuery(id+"F1.opExtrude","SWEPT_FACE",FACE,{"disambiguationData":[OSD([subQ6])]})])],"derivedFrom":makeQuery(id+"F1.opExtrude","CAP_FACE",FACE,{"disambiguationData":[OSD([subQ6,subQ8,subQ9,subQ7,subQ4,subQ3,subQ2,subQ1,subQ0,subQ5,subQ10,subQ11])],"isStart":true})});}
            var sketch = newSketch(context, id + "F15", { "sketchPlane" : qUnion([Q0])});
            skLineSegment(sketch, "E79", {"start": v(-27.73, 90) * mm, "end": v(-15, 102.73) * mm});
            skLineSegment(sketch, "E80", {"start": v(27.73, 90) * mm, "end": v(15, 102.73) * mm});
            skLineSegment(sketch, "E81", {"start": v(-15, 102.73) * mm, "end": v(-15, 114.73) * mm});
            skLineSegment(sketch, "E82", {"start": v(15, 102.73) * mm, "end": v(15, 114.73) * mm});
            skArc(sketch, "E83", {"start": v(0, 129.73) * mm, "mid": v(-10.6, 125.33) * mm, "end": v(-15, 114.73) * mm});
            skArc(sketch, "E84", {"start": v(15, 114.73) * mm, "mid": v(10.6, 125.33) * mm, "end": v(0, 129.73) * mm});
            skCircle(sketch, "E85", {"center": v(0, 114.73) * mm, "radius": 6 * mm});
            skLineSegment(sketch, "E86", {"start": v(-80, 0) * mm, "end": v(80, 0) * mm, "construction": true});
            skLineSegment(sketch, "E87.MirrorCS", {"start": v(-27.73, -90) * mm, "end": v(-15, -102.73) * mm});
            skLineSegment(sketch, "E88.MirrorCS", {"start": v(-15, -102.73) * mm, "end": v(-15, -114.73) * mm});
            skArc(sketch, "E89.MirrorCS", {"start": v(0, -129.73) * mm, "mid": v(-10.6, -125.33) * mm, "end": v(-15, -114.73) * mm});
            skArc(sketch, "E90.MirrorCS", {"start": v(15, -114.73) * mm, "mid": v(10.6, -125.33) * mm, "end": v(0, -129.73) * mm});
            skLineSegment(sketch, "E91.MirrorCS", {"start": v(15, -102.73) * mm, "end": v(15, -114.73) * mm});
            skLineSegment(sketch, "E92.MirrorCS", {"start": v(27.73, -90) * mm, "end": v(15, -102.73) * mm});
            skCircle(sketch, "E93.MirrorC", {"center": v(0, -114.73) * mm, "radius": 6 * mm});
            skSolve(sketch);
        }
        {
            var Q0;
            {var subQ1=sQuery(id+"F15.wireOp",EDGE,"E79");Q0=makeQuery(id+"F15.imprint","IMPRINT",FACE,{"disambiguationData":[TD([[makeQuery(id+"F15.imprint","IMPRINT",EDGE,{"derivedFrom":subQ1}),-1.0]])]});}
            var Q1;
            Q1=makeQuery(id+"F15.imprint","IMPRINT",FACE,{"disambiguationData":[TD([[makeQuery(id+"F15.imprint","IMPRINT",EDGE,{"derivedFrom":makeQuery(id+"F1.opExtrude","CAP_EDGE",EDGE,{"disambiguationData":[OSD([sQuery(id+"F0.wireOp",EDGE,"E1.left")])],"isStart":true})}),-1.0]])]});
            var Q2;
            {var subQ0=sQuery(id+"F15.wireOp",EDGE,"E87.MirrorCS");Q2=makeQuery(id+"F15.imprint","IMPRINT",FACE,{"disambiguationData":[TD([[makeQuery(id+"F15.imprint","IMPRINT",EDGE,{"derivedFrom":subQ0}),1.0]])]});}
            var Q3;
            Q3=makeQuery(id+"F2.opExtrude","CAP_FACE",FACE,{"disambiguationData":[OSD([sQuery(id+"F0.wireOp",EDGE,"E12"),sQuery(id+"F0.wireOp",EDGE,"E13"),sQuery(id+"F0.wireOp",EDGE,"E14"),sQuery(id+"F0.wireOp",EDGE,"E15"),sQuery(id+"F0.wireOp",EDGE,"E17.filletArc"),sQuery(id+"F0.wireOp",EDGE,"E18.filletArc"),sQuery(id+"F0.wireOp",EDGE,"E19.filletArc"),sQuery(id+"F0.wireOp",EDGE,"E20.filletArc"),sQuery(id+"F0.wireOp",EDGE,"E25.0"),sQuery(id+"F0.wireOp",EDGE,"E25.1"),sQuery(id+"F0.wireOp",EDGE,"E25.2"),sQuery(id+"F0.wireOp",EDGE,"E25.3"),sQuery(id+"F0.wireOp",EDGE,"E25.4"),sQuery(id+"F0.wireOp",EDGE,"E25.5"),sQuery(id+"F0.wireOp",EDGE,"E25.6"),sQuery(id+"F0.wireOp",EDGE,"E25.7")])],"isStart":false});
            extrude(context, id + "F16", {"entities" : qUnion([Q0, Q1, Q2]), "endBound" : BoundingType.UP_TO_SURFACE, "depth" : 25 * mm, "endBoundEntityFace" : qUnion([Q3]), "offsetDistance" : 25 * mm});
        }
    });
